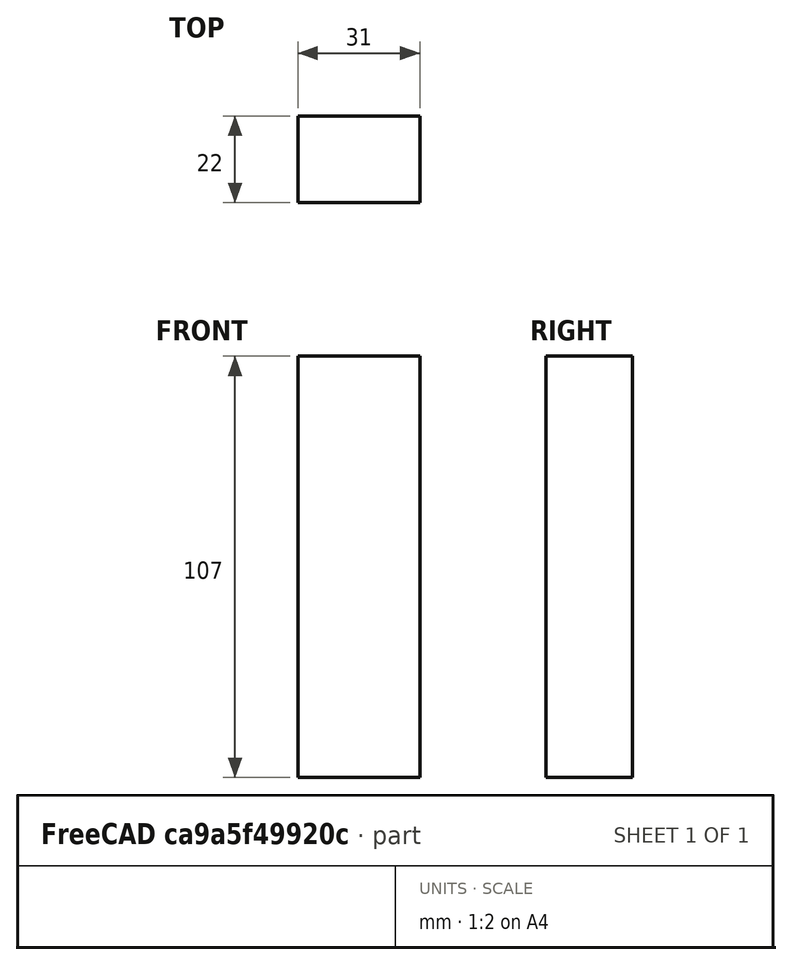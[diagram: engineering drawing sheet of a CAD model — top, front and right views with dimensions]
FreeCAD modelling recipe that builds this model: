
FCSTD DOCUMENT  (FreeCAD 0.16R6712 (Git))
Label: Batterie
License: All rights reserved
LicenseURL: http://en.wikipedia.org/wiki/All_rights_reserved
objects: Sketcher::SketchObject×1, PartDesign::Pad×1
note: 3 computed .brp shape members not serialized (recipe doc carries the construction recipe); baked Part::Feature solids carry a one-line shape summary decoded from their .brp

FEATURE [Sketcher::SketchObject] Sketch
  sketch-geometry (4):
    g0: LineSegment StartX=0 StartY=22 StartZ=0 EndX=31 EndY=22 EndZ=0
    g1: LineSegment StartX=31 StartY=22 StartZ=0 EndX=31 EndY=0 EndZ=0
    g2: LineSegment StartX=31 StartY=0 StartZ=0 EndX=0 EndY=0 EndZ=0
    g3: LineSegment StartX=0 StartY=0 StartZ=0 EndX=0 EndY=22 EndZ=0
  constraints (11):
    c: Coincident(g0,g1)
    c: Coincident(g1,g2)
    c: Coincident(g2,g3)
    c: Coincident(g3,g0)
    c: Horizontal(g0)
    c: Horizontal(g2)
    c: Vertical(g1)
    c: Vertical(g3)
    c: Coincident(g2,g-1)
    c: DistanceX(g2,g2) = 31
    c: DistanceY(g3,g3) = 22
FEATURE [PartDesign::Pad] Pad
  Length = 107
  Length2 = 100
  Sketch = -> Sketch
  Type = 0
